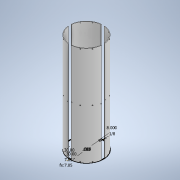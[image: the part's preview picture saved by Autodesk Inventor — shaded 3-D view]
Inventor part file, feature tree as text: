
AUTODESK INVENTOR PART (.ipt)
format: ipt  version: 2021 (Build 250183000, 183)  size: 347,136 bytes
history: native  units: in
note: dims shown in document units (in); Inventor stores cm internally (conversion verified against a paired STEP export)
features: other x24, pattern_circular x6, hole x6, sketch x5, plane x3, extrude x2
ambient origin geometry x8: Origin, YZ Plane, XZ Plane, XY Plane, X Axis, Y Axis, Z Axis, Center Point
bodies: Solid1 (feature_tree)
feature tree (46):
  extrude  "Extrusion1"  TaperAngle=0.0deg  [1 undecoded]
  plane  "Work Plane1"
  extrude  "Extrusion2"  Depth=0.3937in TaperAngle=0.0deg
  pattern_circular  "Circular Pattern1"  Count=4 Angle=360.0deg
  other  "Work Axis1"
  other  "Work Axis2"
  other  "Work Axis3"
  other  "Work Axis4"
  other  "Work Point1"
  other  "Work Point2"
  other  "Work Point3"
  other  "Central Plane"
  other  "Work Point4"
  other  "Work Axis6"
  other  "Work Axis7"
  other  "Offset Plane A"
  other  "Work Point5"
  other  "Work Point6"
  other  "Work Axis8"
  other  "Work Axis9"
  other  "Work Point7"
  other  "Work Point8"
  plane  "Work Plane5"
  plane  "Work Plane6"
  hole  "Hole1"  [1 undecoded]
  hole  "Hole2"  [1 undecoded]
  pattern_circular  "Circular Pattern3"  Count=4 Angle=360.0deg
  sketch  "Sketch5"  dims[d13=0.0484in d14=-11.811in]
  other  "Work Axis10"
  other  "plane for insert hole 1"
  sketch  "Sketch7"  dims[d15=0.0484in d16=0.1574in]
  other  "plane for insert hole 2"
  sketch  "Sketch8"  dims[d17=-0.1574in d48=1.0in d49=1.0in d29=0.096in d30=0.75in d31=0.185in d32=0.25in d33=0.5635in d34=1.0in d35=0.0in d52=1.0in d53=1.0in d38=0.096in d39=0.75in d40=0.185in d41=0.25in d42=0.5635in d43=1.0in d44=0.8108in d45=1.5748in d46=360.0deg d88=30.0deg d89=30.0deg d90=0.0in d91=0.0in d92=0.0in d93=11.811in d94=0.0in d95=11.811in d96=0.129in d97=0.224in d98=0.225in d99=0.25in d100=0.5635in d101=0.349in d102=0.8108in d103=0.129in d104=0.224in d105=0.225in d106=0.25in d107=0.5635in d108=0.349in d109=0.8108in d110=1.5748in d111=360.0deg d116=1.5748in d117=360.0deg d119=0.0in d120=0.0in d121=0.0in d122=0.1969in d123=0.1969in d124=0.0in d125=0.0in d126=0.1969in d127=0.1969in d128=0.129in d129=0.75in d130=0.225in d131=0.25in d132=0.5635in d133=0.349in d134=0.8108in d135=0.129in d136=0.75in d137=0.225in d138=0.25in d139=0.5635in d140=0.349in d141=0.8108in d142=1.5748in d143=360.0deg d145=1.5748in d146=360.0deg d54=1.0in d55=1.0in d56=1.0in d57=0.15in d58=0.25in d59=0.375in d60=0.5635in d61=0.75in d62=0.8108in d63=0.0625in d64=0.75in d65=0.375in]
  hole  "insert hole 2"  [1 undecoded]
  hole  "insert hole 1"  [1 undecoded]
  pattern_circular  "Circular Pattern7"  [2 undecoded]
  pattern_circular  "Circular Pattern9"  [2 undecoded]
  other  "Work Axis14"
  hole  "Hole8"  [1 undecoded]
  hole  "Hole9"  [1 undecoded]
  pattern_circular  "Circular Pattern10"  [2 undecoded]
  pattern_circular  "Circular Pattern11"  Count=30  [1 undecoded]
  sketch  "Sketch1"  dims[d3=0.0in d5=0.0in]
  sketch  "Sketch2"  dims[d7=0.3937in d8=0.5in d9=0.0in d10=1.5748in d11=360.0deg]
  other  "Work Axis5"
  other  "Offset Plane B"
note: 14 required parameter values undecoded (feature->parameter linkage not recoverable at this tier; creation-order binding heuristic only, values carry confidence <= 0.55)
